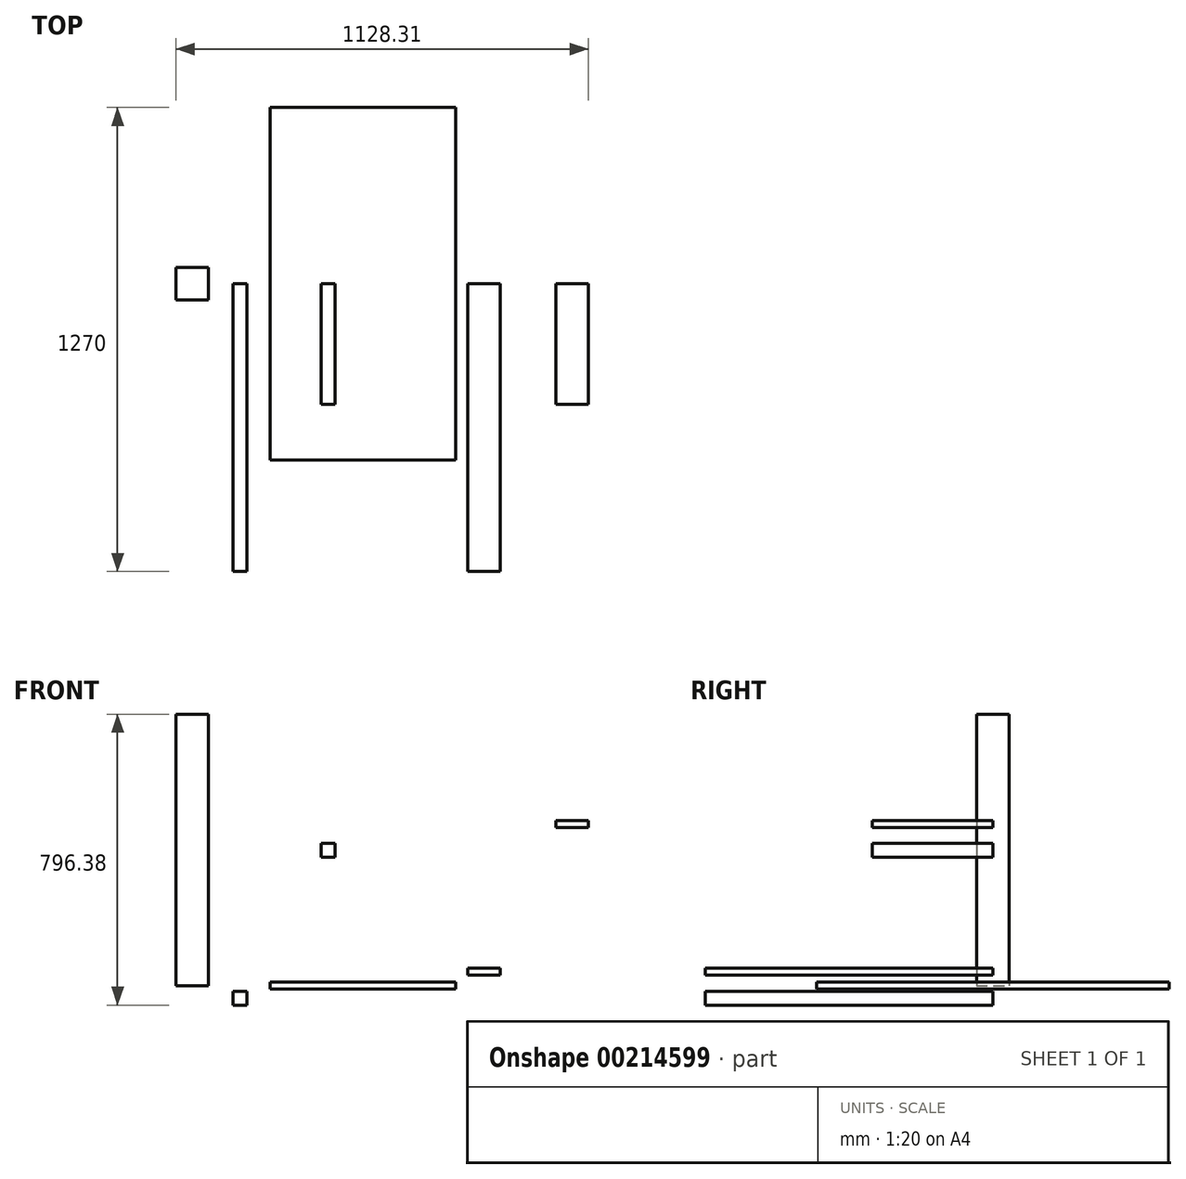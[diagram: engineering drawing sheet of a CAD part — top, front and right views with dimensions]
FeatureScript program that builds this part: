
annotation { "Feature Type Name" : "Feature", "Feature Type Description" : "" }
export const myFeature = defineFeature(function(context is Context, id is Id, definition is map)
    precondition{}
    {
        {
            var Q0;
            Q0=qCreatedBy(makeId("Front.planeOp"),FACE);
            var sketch = newSketch(context, id + "F0", { "sketchPlane" : qUnion([Q0])});
            skLineSegment(sketch, "E0.bottom", {"start": v(254, 9.53) * mm, "end": v(-254, 9.52) * mm});
            skLineSegment(sketch, "E0.top", {"start": v(254, -9.52) * mm, "end": v(-254, -9.53) * mm});
            skLineSegment(sketch, "E0.left", {"start": v(254, 9.53) * mm, "end": v(254, -9.52) * mm});
            skLineSegment(sketch, "E0.right", {"start": v(-254, 9.52) * mm, "end": v(-254, -9.53) * mm});
            skPoint(sketch, "E0.middle", {"position": v(0, 0) * mm});
            skSolve(sketch);
        }
        {
            var Q0;
            Q0 = qSketchRegion(id + "F0", true);
            extrude(context, id + "F1", {"entities" : qUnion([Q0]), "depth" : 482.6 * mm, "hasSecondDirection" : true, "secondDirectionOppositeDirection" : true, "secondDirectionDepth" : 482.6 * mm});
        }
        {
            var Q0;
            Q0=qCreatedBy(makeId("Top.planeOp"),FACE);
            var sketch = newSketch(context, id + "F2", { "sketchPlane" : qUnion([Q0])});
            skLineSegment(sketch, "E1.bottom", {"start": v(-422.9, -44.45) * mm, "end": v(-511.8, -44.45) * mm});
            skLineSegment(sketch, "E1.top", {"start": v(-422.9, 44.45) * mm, "end": v(-511.8, 44.45) * mm});
            skLineSegment(sketch, "E1.left", {"start": v(-422.9, -44.45) * mm, "end": v(-422.9, 44.45) * mm});
            skLineSegment(sketch, "E1.right", {"start": v(-511.8, -44.45) * mm, "end": v(-511.8, 44.45) * mm});
            skPoint(sketch, "E1.middle", {"position": v(-467.36, 0) * mm});
            skSolve(sketch);
        }
        {
            var Q0;
            Q0 = qSketchRegion(id + "F2", true);
            extrude(context, id + "F3", {"entities" : qUnion([Q0]), "depth" : 742.95 * mm});
        }
        {
            var Q0;
            Q0=qCreatedBy(makeId("Front.planeOp"),FACE);
            var sketch = newSketch(context, id + "F4", { "sketchPlane" : qUnion([Q0])});
            skLineSegment(sketch, "E2.bottom", {"start": v(527.6, 452) * mm, "end": v(616.5, 452) * mm});
            skLineSegment(sketch, "E2.top", {"start": v(527.6, 432.96) * mm, "end": v(616.5, 432.96) * mm});
            skLineSegment(sketch, "E2.left", {"start": v(527.6, 452) * mm, "end": v(527.6, 432.96) * mm});
            skLineSegment(sketch, "E2.right", {"start": v(616.5, 452) * mm, "end": v(616.5, 432.96) * mm});
            skLineSegment(sketch, "E3.bottom", {"start": v(-114.92, 389.6) * mm, "end": v(-76.82, 389.6) * mm});
            skLineSegment(sketch, "E3.top", {"start": v(-114.92, 351.5) * mm, "end": v(-76.82, 351.5) * mm});
            skLineSegment(sketch, "E3.left", {"start": v(-114.92, 389.6) * mm, "end": v(-114.92, 351.5) * mm});
            skLineSegment(sketch, "E3.right", {"start": v(-76.82, 389.6) * mm, "end": v(-76.82, 351.5) * mm});
            skSolve(sketch);
        }
        {
            var Q0;
            Q0 = qSketchRegion(id + "F4", true);
            extrude(context, id + "F5", {"entities" : qUnion([Q0]), "depth" : 330.2 * mm});
        }
        {
            var Q0;
            Q0=qCreatedBy(makeId("Front.planeOp"),FACE);
            var sketch = newSketch(context, id + "F6", { "sketchPlane" : qUnion([Q0])});
            skLineSegment(sketch, "E4.bottom", {"start": v(286.34, 47.08) * mm, "end": v(375.24, 47.08) * mm});
            skLineSegment(sketch, "E4.top", {"start": v(286.34, 28.03) * mm, "end": v(375.24, 28.03) * mm});
            skLineSegment(sketch, "E4.left", {"start": v(286.34, 47.08) * mm, "end": v(286.34, 28.03) * mm});
            skLineSegment(sketch, "E4.right", {"start": v(375.24, 47.08) * mm, "end": v(375.24, 28.03) * mm});
            skLineSegment(sketch, "E5.bottom", {"start": v(-356.19, -15.33) * mm, "end": v(-318.09, -15.33) * mm});
            skLineSegment(sketch, "E5.top", {"start": v(-356.19, -53.43) * mm, "end": v(-318.09, -53.43) * mm});
            skLineSegment(sketch, "E5.left", {"start": v(-356.19, -15.33) * mm, "end": v(-356.19, -53.43) * mm});
            skLineSegment(sketch, "E5.right", {"start": v(-318.09, -15.33) * mm, "end": v(-318.09, -53.43) * mm});
            skSolve(sketch);
        }
        {
            var Q0;
            Q0=makeQuery(id+"F6.imprint","IMPRINT",FACE,{"disambiguationData":[TD([[makeQuery(id+"F6.imprint","IMPRINT",EDGE,{"derivedFrom":sQuery(id+"F6.wireOp",EDGE,"E5.bottom")}),-1.0]])]});
            var Q1;
            Q1=makeQuery(id+"F6.imprint","IMPRINT",FACE,{"disambiguationData":[TD([[makeQuery(id+"F6.imprint","IMPRINT",EDGE,{"derivedFrom":sQuery(id+"F6.wireOp",EDGE,"E4.bottom")}),-1.0]])]});
            var Q2;
            Q2=sQuery(id+"F6.wireOp",EDGE,"E4.bottom");
            var Q3;
            Q3=sQuery(id+"F6.wireOp",EDGE,"E4.top");
            var Q4;
            Q4=sQuery(id+"F6.wireOp",EDGE,"E4.left");
            var Q5;
            Q5=sQuery(id+"F6.wireOp",EDGE,"E4.right");
            var Q6;
            Q6=sQuery(id+"F6.wireOp",EDGE,"E5.bottom");
            var Q7;
            Q7=sQuery(id+"F6.wireOp",EDGE,"E5.top");
            var Q8;
            Q8=sQuery(id+"F6.wireOp",EDGE,"E5.left");
            var Q9;
            Q9=sQuery(id+"F6.wireOp",EDGE,"E5.right");
            extrude(context, id + "F7", {"entities" : qUnion([Q0, Q1]), "surfaceEntities" : qUnion([Q2, Q3, Q4, Q5, Q6, Q7, Q8, Q9]), "depth" : 787.4 * mm});
        }
    });
